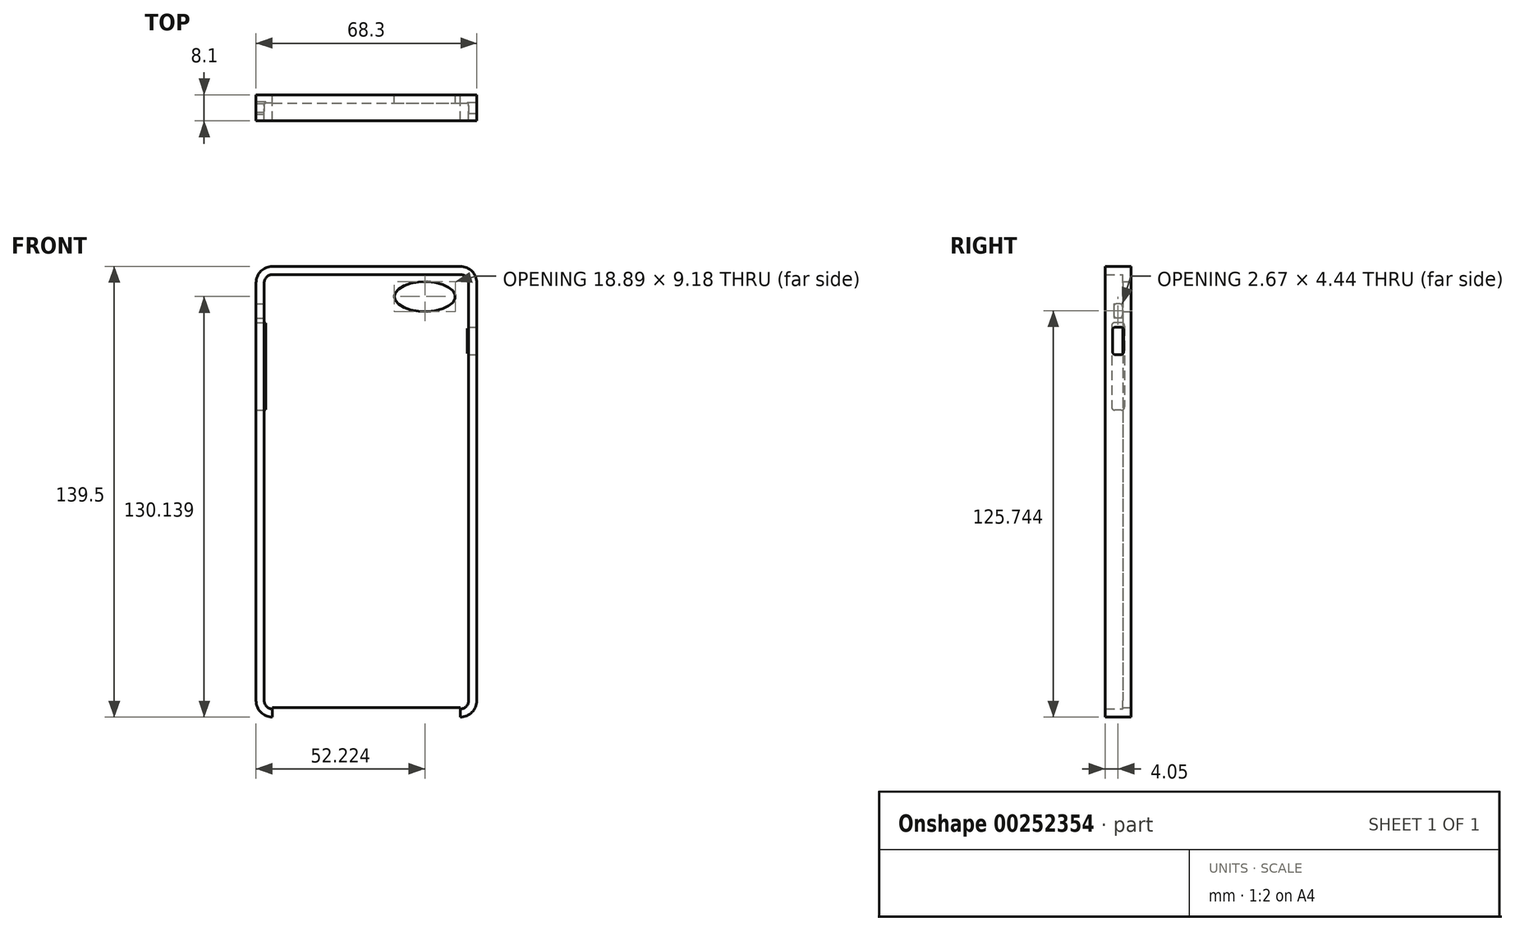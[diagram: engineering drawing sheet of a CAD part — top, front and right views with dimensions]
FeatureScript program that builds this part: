
annotation { "Feature Type Name" : "Feature", "Feature Type Description" : "" }
export const myFeature = defineFeature(function(context is Context, id is Id, definition is map)
    precondition{}
    {
        {
            var Q0;
            Q0=qCreatedBy(makeId("Front.planeOp"),FACE);
            var sketch = newSketch(context, id + "F0", { "sketchPlane" : qUnion([Q0])});
            skLineSegment(sketch, "E0.bottom", {"start": v(34.15, 69.75) * mm, "end": v(-34.15, 69.75) * mm});
            skLineSegment(sketch, "E0.top", {"start": v(34.15, -69.75) * mm, "end": v(-34.15, -69.75) * mm});
            skLineSegment(sketch, "E0.left", {"start": v(34.15, 69.75) * mm, "end": v(34.15, -69.75) * mm});
            skLineSegment(sketch, "E0.right", {"start": v(-34.15, 69.75) * mm, "end": v(-34.15, -69.75) * mm});
            skPoint(sketch, "E0.middle", {"position": v(0, 0) * mm});
            skSolve(sketch);
        }
        {
            var Q0;
            Q0=makeQuery(id+"F0.imprint","IMPRINT",FACE,{"disambiguationData":[TD([[makeQuery(id+"F0.imprint","IMPRINT",EDGE,{"derivedFrom":sQuery(id+"F0.wireOp",EDGE,"E0.bottom")}),1.0]])]});
            extrude(context, id + "F1", {"entities" : qUnion([Q0]), "endBound" : BoundingType.SYMMETRIC, "depth" : 8.1 * mm});
        }
        {
            var Q0;
            Q0=makeQuery(id+"F1.opExtrude","SWEPT_EDGE",EDGE,{"disambiguationData":[OSD([sQuery(id+"F0.wireOp",EDGE,"E0.bottom"),sQuery(id+"F0.wireOp",EDGE,"E0.right")])]});
            var Q1;
            Q1=makeQuery(id+"F1.opExtrude","SWEPT_EDGE",EDGE,{"disambiguationData":[OSD([sQuery(id+"F0.wireOp",EDGE,"E0.bottom"),sQuery(id+"F0.wireOp",EDGE,"E0.left")])]});
            var Q2;
            Q2=makeQuery(id+"F1.opExtrude","SWEPT_EDGE",EDGE,{"disambiguationData":[OSD([sQuery(id+"F0.wireOp",EDGE,"E0.top"),sQuery(id+"F0.wireOp",EDGE,"E0.left")])]});
            var Q3;
            Q3=makeQuery(id+"F1.opExtrude","SWEPT_EDGE",EDGE,{"disambiguationData":[OSD([sQuery(id+"F0.wireOp",EDGE,"E0.top"),sQuery(id+"F0.wireOp",EDGE,"E0.right")])]});
            fillet(context, id + "F2", {"entities" : qUnion([Q0, Q1, Q2, Q3]), "radius" : 5.08 * mm, "tangentPropagation" : true, "allowEdgeOverflow" : false});
        }
        {
            var Q0;
            Q0=makeQuery(id+"F1.opExtrude","CAP_FACE",FACE,{"disambiguationData":[OSD([sQuery(id+"F0.wireOp",EDGE,"E0.bottom"),sQuery(id+"F0.wireOp",EDGE,"E0.top"),sQuery(id+"F0.wireOp",EDGE,"E0.left"),sQuery(id+"F0.wireOp",EDGE,"E0.right")])],"isStart":false});
            var Q1;
            Q1=makeQuery(id+"F1.opExtrude","SWEPT_BODY",BODY,{"disambiguationData":[OSD([sQuery(id+"F0.wireOp",EDGE,"E0.bottom"),sQuery(id+"F0.wireOp",EDGE,"E0.top"),sQuery(id+"F0.wireOp",EDGE,"E0.left"),sQuery(id+"F0.wireOp",EDGE,"E0.right")])]});
            shell(context, id + "F3", {"entities" : qUnion([Q0]), "parts" : qUnion([Q1]), "thickness" : 2.54 * mm});
        }
        {
            var Q0;
            Q0=makeQuery(id+"F3.opShell","OFFSET_FACE",FACE,{"disambiguationData":[OSD([sQuery(id+"F0.wireOp",EDGE,"E0.bottom"),sQuery(id+"F0.wireOp",EDGE,"E0.top"),sQuery(id+"F0.wireOp",EDGE,"E0.left"),sQuery(id+"F0.wireOp",EDGE,"E0.right")])]});
            var sketch = newSketch(context, id + "F4", { "sketchPlane" : qUnion([Q0])});
            skEllipse(sketch, "E1", {"center": v(18.07, 60.39) * mm, "majorRadius": 9.45 * mm, "minorRadius": 4.59 * mm, "majorAxis": v(-1, 0)});
            skSolve(sketch);
        }
        {
            var Q0;
            Q0=makeQuery(id+"F4.imprint","IMPRINT",FACE,{"disambiguationData":[TD([[makeQuery(id+"F4.imprint","IMPRINT",EDGE,{"derivedFrom":sQuery(id+"F4.wireOp",EDGE,"E1")}),1.0]])]});
            extrude(context, id + "F5", {"entities" : qUnion([Q0]), "operationType" : NewBodyOperationType.REMOVE, "endBound" : BoundingType.SYMMETRIC, "depth" : 60 * mm});
        }
        {
            var Q0;
            Q0=makeQuery(id+"F1.opExtrude","SWEPT_FACE",FACE,{"disambiguationData":[OSD([sQuery(id+"F0.wireOp",EDGE,"E0.right")])]});
            var sketch = newSketch(context, id + "F6", { "sketchPlane" : qUnion([Q0])});
            skSolve(sketch);
        }
        {
            var Q0;
            Q0=makeQuery(id+"F1.opExtrude","SWEPT_FACE",FACE,{"disambiguationData":[OSD([sQuery(id+"F0.wireOp",EDGE,"E0.top")])]});
            var sketch = newSketch(context, id + "F7", { "sketchPlane" : qUnion([Q0])});
            skLineSegment(sketch, "E2", {"start": v(-12.62, -4.05) * mm, "end": v(19.5, -4.05) * mm});
            skLineSegment(sketch, "E3", {"start": v(19.5, -4.05) * mm, "end": v(19.5, 4.05) * mm});
            skLineSegment(sketch, "E4", {"start": v(19.5, 4.05) * mm, "end": v(-12.62, 4.05) * mm});
            skLineSegment(sketch, "E5", {"start": v(-12.62, 4.05) * mm, "end": v(-12.62, -4.05) * mm});
            skSolve(sketch);
        }
        {
            var Q0;
            Q0=makeQuery(id+"F7.imprint","IMPRINT",FACE,{"disambiguationData":[TD([[makeQuery(id+"F7.imprint","IMPRINT",EDGE,{"derivedFrom":sQuery(id+"F7.wireOp",EDGE,"E2")}),-1.0]])]});
            extrude(context, id + "F8", {"entities" : qUnion([Q0]), "operationType" : NewBodyOperationType.REMOVE, "endBound" : BoundingType.SYMMETRIC, "oppositeDirection" : true, "depth" : 6 * mm});
        }
        {
            var Q0;
            Q0=makeQuery(id+"F1.opExtrude","SWEPT_FACE",FACE,{"disambiguationData":[OSD([sQuery(id+"F0.wireOp",EDGE,"E0.left")])]});
            var sketch = newSketch(context, id + "F9", { "sketchPlane" : qUnion([Q0])});
            skLineSegment(sketch, "E6.bottom", {"start": v(1.72, 42.37) * mm, "end": v(-1.72, 42.37) * mm});
            skLineSegment(sketch, "E6.top", {"start": v(1.72, 50.97) * mm, "end": v(-1.72, 50.97) * mm});
            skLineSegment(sketch, "E6.left", {"start": v(1.72, 42.37) * mm, "end": v(1.72, 50.97) * mm});
            skLineSegment(sketch, "E6.right", {"start": v(-1.72, 42.37) * mm, "end": v(-1.72, 50.97) * mm});
            skPoint(sketch, "E6.middle", {"position": v(0, 46.67) * mm});
            skSolve(sketch);
        }
        {
            var Q0;
            Q0=makeQuery(id+"F9.imprint","IMPRINT",FACE,{"disambiguationData":[TD([[makeQuery(id+"F9.imprint","IMPRINT",EDGE,{"derivedFrom":sQuery(id+"F9.wireOp",EDGE,"E6.bottom")}),-1.0]])]});
            extrude(context, id + "F10", {"entities" : qUnion([Q0]), "operationType" : NewBodyOperationType.REMOVE, "endBound" : BoundingType.SYMMETRIC, "oppositeDirection" : true, "depth" : 6 * mm});
        }
        {
            var Q0;
            {var subQ0=sQuery(id+"F0.wireOp",EDGE,"E0.right");Q0=makeQuery(id+"F6.imprint","IMPRINT",FACE,{"disambiguationData":[TD([[makeQuery(id+"F6.imprint","IMPRINT",EDGE,{"derivedFrom":makeQuery(id+"F1.opExtrude","CAP_EDGE",EDGE,{"disambiguationData":[OSD([subQ0])],"isStart":true})}),1.0]])]});}
            var sketch = newSketch(context, id + "F11", { "sketchPlane" : qUnion([Q0])});
            skLineSegment(sketch, "E7.bottom", {"start": v(-1.33, 58.21) * mm, "end": v(1.33, 58.21) * mm});
            skLineSegment(sketch, "E7.top", {"start": v(-1.33, 53.78) * mm, "end": v(1.33, 53.78) * mm});
            skLineSegment(sketch, "E7.left", {"start": v(-1.33, 58.21) * mm, "end": v(-1.33, 53.78) * mm});
            skLineSegment(sketch, "E7.right", {"start": v(1.33, 58.21) * mm, "end": v(1.33, 53.78) * mm});
            skPoint(sketch, "E7.middle", {"position": v(0, 56) * mm});
            skSolve(sketch);
        }
        {
            var Q0;
            Q0 = qSketchRegion(id + "F11", true);
            extrude(context, id + "F12", {"entities" : qUnion([Q0]), "operationType" : NewBodyOperationType.REMOVE, "endBound" : BoundingType.SYMMETRIC, "depth" : 6 * mm});
        }
        {
            var Q0;
            {var subQ0=sQuery(id+"F0.wireOp",EDGE,"E0.right");Q0=makeQuery(id+"F6.imprint","IMPRINT",FACE,{"disambiguationData":[TD([[makeQuery(id+"F6.imprint","IMPRINT",EDGE,{"derivedFrom":makeQuery(id+"F1.opExtrude","CAP_EDGE",EDGE,{"disambiguationData":[OSD([subQ0])],"isStart":true})}),1.0]])]});}
            var sketch = newSketch(context, id + "F13", { "sketchPlane" : qUnion([Q0])});
            skLineSegment(sketch, "E8.bottom", {"start": v(-2.02, 52.3) * mm, "end": v(2.02, 52.3) * mm});
            skLineSegment(sketch, "E8.top", {"start": v(-2.02, 25.26) * mm, "end": v(2.02, 25.26) * mm});
            skLineSegment(sketch, "E8.left", {"start": v(-2.02, 52.3) * mm, "end": v(-2.02, 25.26) * mm});
            skLineSegment(sketch, "E8.right", {"start": v(2.02, 52.3) * mm, "end": v(2.02, 25.26) * mm});
            skPoint(sketch, "E8.middle", {"position": v(0, 38.78) * mm});
            skSolve(sketch);
        }
        {
            var Q0;
            Q0 = qSketchRegion(id + "F13", true);
            extrude(context, id + "F14", {"entities" : qUnion([Q0]), "operationType" : NewBodyOperationType.REMOVE, "endBound" : BoundingType.SYMMETRIC, "depth" : 6 * mm});
        }
        {
            var Q0;
            {var subQ2=sQuery(id+"F0.wireOp",EDGE,"E0.top");Q0=makeQuery(id+"F8.boolean.opBoolean","SPLIT",FACE,{"disambiguationData":[TD([makeQuery(id+"F8.opExtrude","SWEPT_FACE",FACE,{"disambiguationData":[OSD([sQuery(id+"F7.wireOp",EDGE,"E5")])]})])],"derivedFrom":makeQuery(id+"F1.opExtrude","SWEPT_FACE",FACE,{"disambiguationData":[OSD([subQ2])]})});}
            var sketch = newSketch(context, id + "F15", { "sketchPlane" : qUnion([Q0])});
            skSolve(sketch);
        }
        {
            var Q0;
            {var subQ0=sQuery(id+"F0.wireOp",EDGE,"E0.top");var subQ1=makeQuery(id+"F1.opExtrude","SWEPT_FACE",FACE,{"disambiguationData":[OSD([subQ0])]});var subQ6=makeQuery(id+"F8.opExtrude","SWEPT_FACE",FACE,{"disambiguationData":[OSD([sQuery(id+"F7.wireOp",EDGE,"E5")])]});Q0=makeQuery(id+"F15.imprint","IMPRINT",FACE,{"disambiguationData":[TD([[makeQuery(id+"F15.imprint","IMPRINT",EDGE,{"derivedFrom":makeQuery(id+"F8.boolean.opBoolean","INTERSECT",EDGE,{"derivedFrom":[subQ1,subQ6]})}),-1.0]])]});}
            var Q1;
            {var subQ2=sQuery(id+"F0.wireOp",EDGE,"E0.top");Q1=makeQuery(id+"F8.boolean.opBoolean","SPLIT",FACE,{"disambiguationData":[TD([makeQuery(id+"F8.opExtrude","SWEPT_FACE",FACE,{"disambiguationData":[OSD([sQuery(id+"F7.wireOp",EDGE,"E3")])]})])],"derivedFrom":makeQuery(id+"F1.opExtrude","SWEPT_FACE",FACE,{"disambiguationData":[OSD([subQ2])]})});}
            extrude(context, id + "F16", {"entities" : qUnion([Q0, Q1]), "operationType" : NewBodyOperationType.REMOVE, "oppositeDirection" : true, "depth" : 3 * mm});
        }
        {
            var Q0;
            Q0=makeQuery(id+"F10.boolean.opBoolean","COPY",EDGE,{"derivedFrom":makeQuery(id+"F10.opExtrude","SWEPT_EDGE",EDGE,{"disambiguationData":[OSD([sQuery(id+"F9.wireOp",EDGE,"E6.bottom"),sQuery(id+"F9.wireOp",EDGE,"E6.right")])]})});
            var Q1;
            Q1=makeQuery(id+"F10.boolean.opBoolean","COPY",EDGE,{"derivedFrom":makeQuery(id+"F10.opExtrude","SWEPT_EDGE",EDGE,{"disambiguationData":[OSD([sQuery(id+"F9.wireOp",EDGE,"E6.top"),sQuery(id+"F9.wireOp",EDGE,"E6.right")])]})});
            var Q2;
            Q2=makeQuery(id+"F10.boolean.opBoolean","COPY",EDGE,{"derivedFrom":makeQuery(id+"F10.opExtrude","SWEPT_EDGE",EDGE,{"disambiguationData":[OSD([sQuery(id+"F9.wireOp",EDGE,"E6.bottom"),sQuery(id+"F9.wireOp",EDGE,"E6.left")])]})});
            var Q3;
            Q3=makeQuery(id+"F10.boolean.opBoolean","COPY",EDGE,{"derivedFrom":makeQuery(id+"F10.opExtrude","SWEPT_EDGE",EDGE,{"disambiguationData":[OSD([sQuery(id+"F9.wireOp",EDGE,"E6.top"),sQuery(id+"F9.wireOp",EDGE,"E6.left")])]})});
            fillet(context, id + "F17", {"entities" : qUnion([Q0, Q1, Q2, Q3]), "radius" : 1 * mm, "tangentPropagation" : true, "allowEdgeOverflow" : false});
        }
        {
            var Q0;
            Q0=makeQuery(id+"F14.boolean.opBoolean","COPY",EDGE,{"derivedFrom":makeQuery(id+"F14.opExtrude","SWEPT_EDGE",EDGE,{"disambiguationData":[OSD([sQuery(id+"F13.wireOp",EDGE,"E8.top"),sQuery(id+"F13.wireOp",EDGE,"E8.left")])]})});
            var Q1;
            Q1=makeQuery(id+"F14.boolean.opBoolean","COPY",EDGE,{"derivedFrom":makeQuery(id+"F14.opExtrude","SWEPT_EDGE",EDGE,{"disambiguationData":[OSD([sQuery(id+"F13.wireOp",EDGE,"E8.top"),sQuery(id+"F13.wireOp",EDGE,"E8.right")])]})});
            var Q2;
            Q2=makeQuery(id+"F14.boolean.opBoolean","COPY",EDGE,{"derivedFrom":makeQuery(id+"F14.opExtrude","SWEPT_EDGE",EDGE,{"disambiguationData":[OSD([sQuery(id+"F13.wireOp",EDGE,"E8.bottom"),sQuery(id+"F13.wireOp",EDGE,"E8.right")])]})});
            var Q3;
            Q3=makeQuery(id+"F14.boolean.opBoolean","COPY",EDGE,{"derivedFrom":makeQuery(id+"F14.opExtrude","SWEPT_EDGE",EDGE,{"disambiguationData":[OSD([sQuery(id+"F13.wireOp",EDGE,"E8.bottom"),sQuery(id+"F13.wireOp",EDGE,"E8.left")])]})});
            fillet(context, id + "F18", {"entities" : qUnion([Q0, Q1, Q2, Q3]), "radius" : 1 * mm, "tangentPropagation" : true, "allowEdgeOverflow" : false});
        }
        {
            var Q0;
            Q0=makeQuery(id+"F12.boolean.opBoolean","COPY",EDGE,{"derivedFrom":makeQuery(id+"F12.opExtrude","SWEPT_EDGE",EDGE,{"disambiguationData":[OSD([sQuery(id+"F11.wireOp",EDGE,"E7.bottom"),sQuery(id+"F11.wireOp",EDGE,"E7.left")])]})});
            var Q1;
            Q1=makeQuery(id+"F12.boolean.opBoolean","COPY",EDGE,{"derivedFrom":makeQuery(id+"F12.opExtrude","SWEPT_EDGE",EDGE,{"disambiguationData":[OSD([sQuery(id+"F11.wireOp",EDGE,"E7.top"),sQuery(id+"F11.wireOp",EDGE,"E7.left")])]})});
            var Q2;
            Q2=makeQuery(id+"F12.boolean.opBoolean","COPY",EDGE,{"derivedFrom":makeQuery(id+"F12.opExtrude","SWEPT_EDGE",EDGE,{"disambiguationData":[OSD([sQuery(id+"F11.wireOp",EDGE,"E7.top"),sQuery(id+"F11.wireOp",EDGE,"E7.right")])]})});
            var Q3;
            Q3=makeQuery(id+"F12.boolean.opBoolean","COPY",EDGE,{"derivedFrom":makeQuery(id+"F12.opExtrude","SWEPT_EDGE",EDGE,{"disambiguationData":[OSD([sQuery(id+"F11.wireOp",EDGE,"E7.bottom"),sQuery(id+"F11.wireOp",EDGE,"E7.right")])]})});
            fillet(context, id + "F19", {"entities" : qUnion([Q0, Q1, Q2, Q3]), "radius" : 1 * mm, "tangentPropagation" : true, "allowEdgeOverflow" : false});
        }
    });
